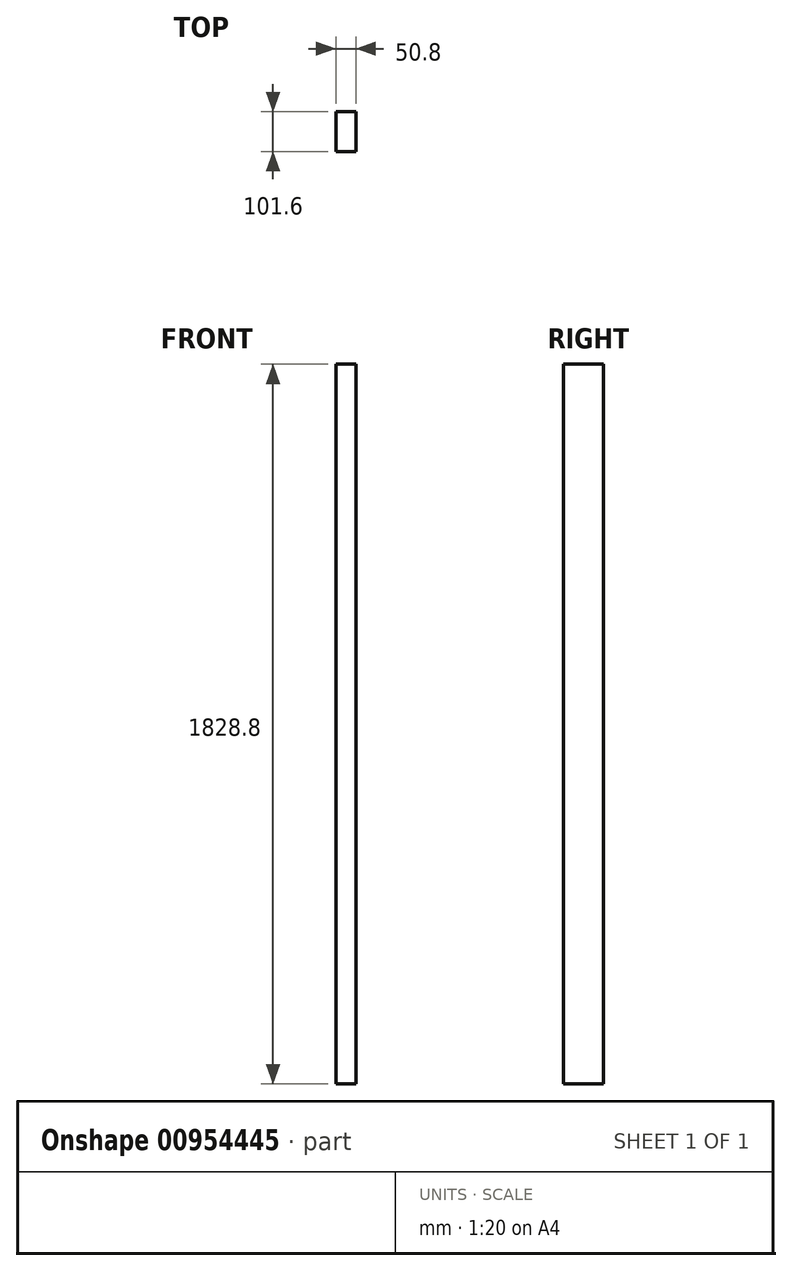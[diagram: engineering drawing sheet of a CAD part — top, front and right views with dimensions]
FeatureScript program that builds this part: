
annotation { "Feature Type Name" : "Feature", "Feature Type Description" : "" }
export const myFeature = defineFeature(function(context is Context, id is Id, definition is map)
    precondition{}
    {
        {
            var Q0;
            Q0=qCreatedBy(makeId("Top.planeOp"),FACE);
            var sketch = newSketch(context, id + "F0", { "sketchPlane" : qUnion([Q0])});
            skLineSegment(sketch, "E0.bottom", {"start": v(0, 0) * mm, "end": v(50.8, 0) * mm});
            skLineSegment(sketch, "E0.top", {"start": v(0, 101.6) * mm, "end": v(50.8, 101.6) * mm});
            skLineSegment(sketch, "E0.left", {"start": v(0, 0) * mm, "end": v(0, 101.6) * mm});
            skLineSegment(sketch, "E0.right", {"start": v(50.8, 0) * mm, "end": v(50.8, 101.6) * mm});
            skSolve(sketch);
        }
        {
            var Q0;
            Q0 = qSketchRegion(id + "F0", true);
            extrude(context, id + "F1", {"entities" : qUnion([Q0]), "depth" : 1828.8 * mm, "offsetDistance" : 25.4 * mm});
        }
    });
